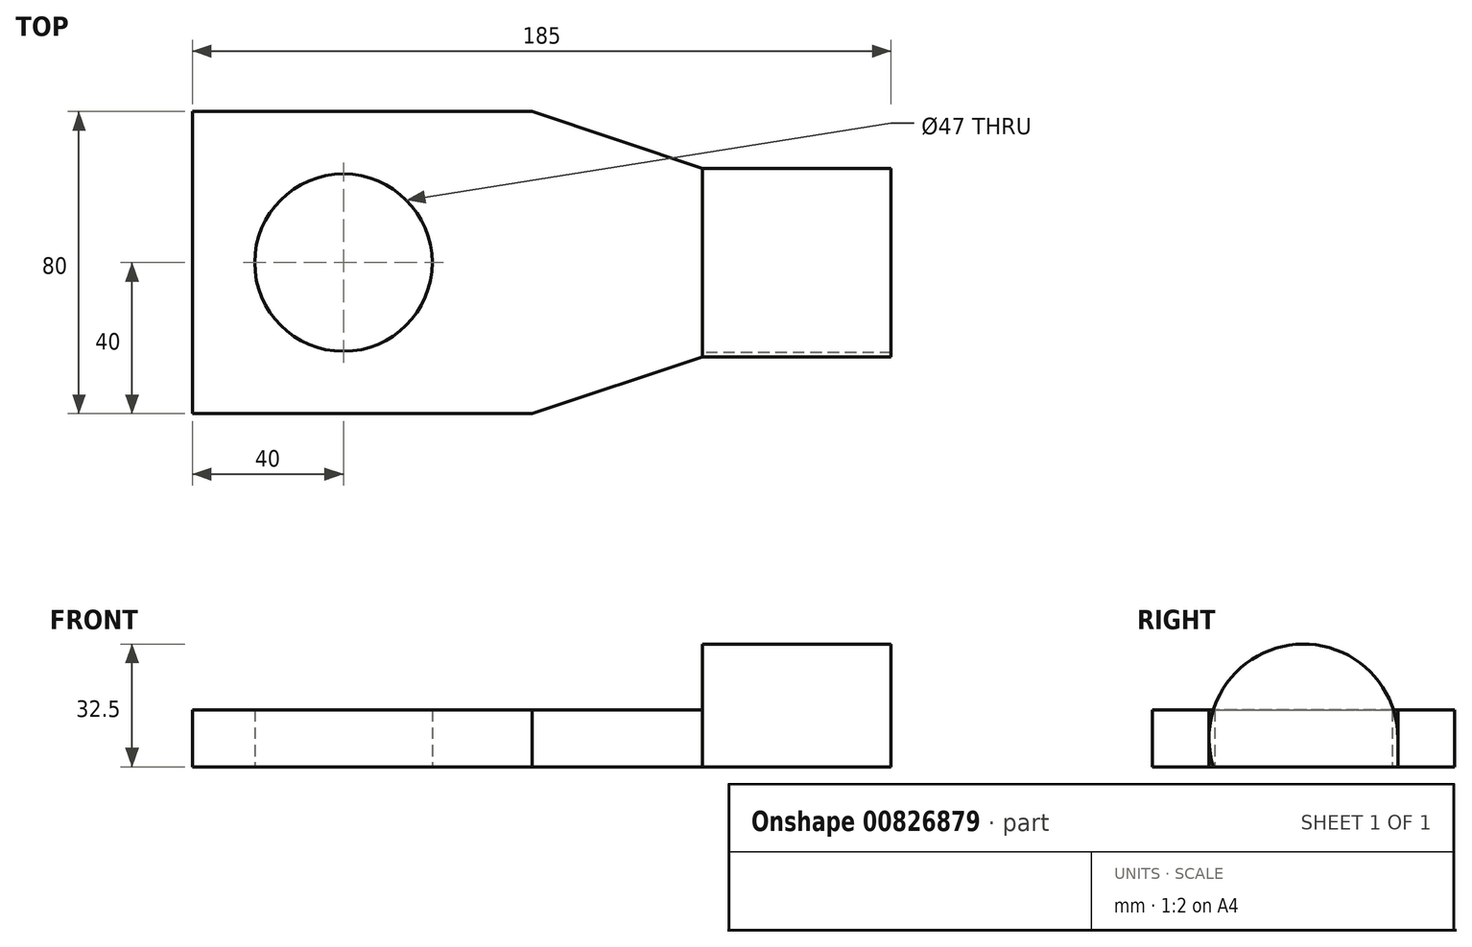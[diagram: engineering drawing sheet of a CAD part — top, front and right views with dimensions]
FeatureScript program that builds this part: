
annotation { "Feature Type Name" : "Feature", "Feature Type Description" : "" }
export const myFeature = defineFeature(function(context is Context, id is Id, definition is map)
    precondition{}
    {
        {
            var Q0;
            Q0=qCreatedBy(makeId("Top.planeOp"),FACE);
            var sketch = newSketch(context, id + "F0", { "sketchPlane" : qUnion([Q0])});
            skLineSegment(sketch, "E0.bottom", {"start": v(0, -40) * mm, "end": v(-90, -40) * mm});
            skLineSegment(sketch, "E0.top", {"start": v(0, 40) * mm, "end": v(-90, 40) * mm});
            skLineSegment(sketch, "E0.right", {"start": v(-90, -40) * mm, "end": v(-90, 40) * mm});
            skPoint(sketch, "E0.middle", {"position": v(0, 0) * mm});
            skCircle(sketch, "E1", {"center": v(-50, 0) * mm, "radius": 23.5 * mm});
            skLineSegment(sketch, "E2", {"start": v(0, 40) * mm, "end": v(45, 25) * mm});
            skLineSegment(sketch, "E3", {"start": v(45, -25) * mm, "end": v(0, -40) * mm});
            skLineSegment(sketch, "E4", {"start": v(45, 25) * mm, "end": v(45, -25) * mm});
            skSolve(sketch);
        }
        {
            var Q0;
            Q0=makeQuery(id+"F0.imprint","IMPRINT",FACE,{"disambiguationData":[TD([[makeQuery(id+"F0.imprint","IMPRINT",EDGE,{"derivedFrom":sQuery(id+"F0.wireOp",EDGE,"E0.bottom")}),-1.0]])]});
            extrude(context, id + "F1", {"entities" : qUnion([Q0]), "depth" : 15 * mm, "offsetDistance" : 25 * mm});
        }
        {
            var Q0;
            Q0=makeQuery(id+"F1.opExtrude","SWEPT_FACE",FACE,{"disambiguationData":[OSD([sQuery(id+"F0.wireOp",EDGE,"E4")])]});
            var sketch = newSketch(context, id + "F2", { "sketchPlane" : qUnion([Q0])});
            skCircle(sketch, "E5", {"center": v(0, 7.5) * mm, "radius": 25 * mm});
            skSolve(sketch);
        }
        {
            var Q0;
            {var subQ0=sQuery(id+"F2.wireOp",EDGE,"E5");var subQ1=makeQuery(id+"F1.opExtrude","CAP_EDGE",EDGE,{"disambiguationData":[OSD([sQuery(id+"F0.wireOp",EDGE,"E4")])],"isStart":false});var subQ2=makeQuery(id+"F2.imprint","INTERSECT",VERTEX,{"disambiguationData":[OD(0.0)],"derivedFrom":[subQ1,subQ0]});Q0=makeQuery(id+"F2.imprint","IMPRINT",FACE,{"disambiguationData":[TD([[makeQuery(id+"F2.imprint","IMPRINT",EDGE,{"disambiguationData":[TD([[subQ2,-1.0]])],"derivedFrom":subQ0}),1.0]])]});}
            var Q1;
            {var subQ0=sQuery(id+"F2.wireOp",EDGE,"E5");var subQ1=makeQuery(id+"F1.opExtrude","CAP_EDGE",EDGE,{"disambiguationData":[OSD([sQuery(id+"F0.wireOp",EDGE,"E4")])],"isStart":true});var subQ2=makeQuery(id+"F2.imprint","INTERSECT",VERTEX,{"disambiguationData":[OD(0.0)],"derivedFrom":[subQ1,subQ0]});Q1=makeQuery(id+"F2.imprint","IMPRINT",FACE,{"disambiguationData":[TD([[makeQuery(id+"F2.imprint","IMPRINT",EDGE,{"disambiguationData":[TD([[subQ2,-1.0]])],"derivedFrom":subQ0}),1.0]])]});}
            var Q2;
            {var subQ0=sQuery(id+"F2.wireOp",EDGE,"E5");var subQ1=sQuery(id+"F0.wireOp",EDGE,"E4");var subQ3=makeQuery(id+"F1.opExtrude","CAP_EDGE",EDGE,{"disambiguationData":[OSD([subQ1])],"isStart":true});var subQ4=makeQuery(id+"F2.imprint","INTERSECT",VERTEX,{"disambiguationData":[OD(0.0)],"derivedFrom":[subQ3,subQ0]});Q2=makeQuery(id+"F2.imprint","IMPRINT",FACE,{"disambiguationData":[TD([[makeQuery(id+"F2.imprint","IMPRINT",EDGE,{"disambiguationData":[TD([[subQ4,1.0]])],"derivedFrom":subQ3}),-1.0]])]});}
            extrude(context, id + "F3", {"entities" : qUnion([Q0, Q1, Q2]), "operationType" : NewBodyOperationType.ADD, "depth" : 50 * mm, "offsetDistance" : 25 * mm});
        }
    });
